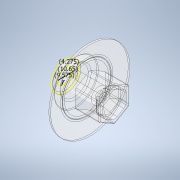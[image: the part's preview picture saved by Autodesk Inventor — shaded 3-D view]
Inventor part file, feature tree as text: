
AUTODESK INVENTOR PART (.ipt)
format: ipt  version: 2020.2 (Build 242310000, 310)  size: 477,696 bytes
history: native  units: mm
features: extrude x5, sketch x4, chamfer x4, revolve x2, fillet x2, other x1, thicken_offset x1, boolean_combine x1, draft x1
ambient origin geometry x8: Origin, YZ Plane, XZ Plane, XY Plane, X Axis, Y Axis, Z Axis, Center Point
bodies: Solid2 (feature_tree), Solid3 (feature_tree)
feature tree (21):
  sketch  "Sketch1"  dims[d0=30.0mm d42=7.4mm]
  sketch  "Sketch8"  dims[d43=7.0mm d44=30.0mm]
  sketch  "Sketch9"  dims[d45=90.0deg d46=10.0mm]
  revolve  "Revolution2"  [1 undecoded]
  extrude  "Extrusion10"  Depth=7.0mm
  extrude  "Extrusion12"  Depth=10.0mm
  extrude  "Extrusion8"  Depth=0.4mm
  extrude  "Extrusion9"  Depth=20.0mm TaperAngle=0.0deg
  chamfer  "Chamfer1"  Distance=10.0mm
  chamfer  "Chamfer3"  Distance=1.0mm Angle=45.0deg
  chamfer  "Chamfer5"  Distance=19.2mm
  extrude  "Extrusion11"  Depth=20.0mm
  fillet  "Fillet2"  Radius=16.6mm
  chamfer  "Chamfer4"  Distance=0.2mm
  fillet  "Fillet1"  Radius=1.2mm
  other  "Thicken1_compensate_shinkage"
  thicken_offset  "Thicken3"
  revolve  "Revolution4"  [1 undecoded]
  boolean_combine  "Combine1"
  draft  "FaceDraft1"
  sketch  "Sketch11"  dims[d47=4.0mm d48=5.3mm d49=20.0mm d50=0.0mm d51=10.0mm d52=0.0mm d56=1.0mm d57=2.0mm d58=45.0deg d62=19.2mm d65=20.0mm d66=16.6mm d67=0.2mm d68=1.2mm d73=1.6mm d75=0.5mm d76=2.0mm d77=45.0deg d79=54.0mm d80=20.5mm d81=10.0mm d82=0.0mm d83=16.0mm d84=8.0mm d85=0.0mm d86=1.2mm d88=1.0mm d89=0.325mm d90=0.1mm d91=3.5mm d92=2.0mm d93=45.0deg d94=3.5mm d97=3.0mm d98=0.0mm d99=1.2mm d100=2.6mm d101=1.4mm d102=23.0mm d103=90.0deg d104=10.6mm d105=0.25mm d106=0.1mm d107=9.575mm d108=10.65mm d109=4.275mm d110=0.6mm d111=2.0mm d112=45.0deg d113=0.349066mm d114=0.4mm d15=0.5mm d16=0.872665mm d17=0.5mm d18=0.872665mm]
note: 2 required parameter values undecoded (feature->parameter linkage not recoverable at this tier; creation-order binding heuristic only, values carry confidence <= 0.55)
